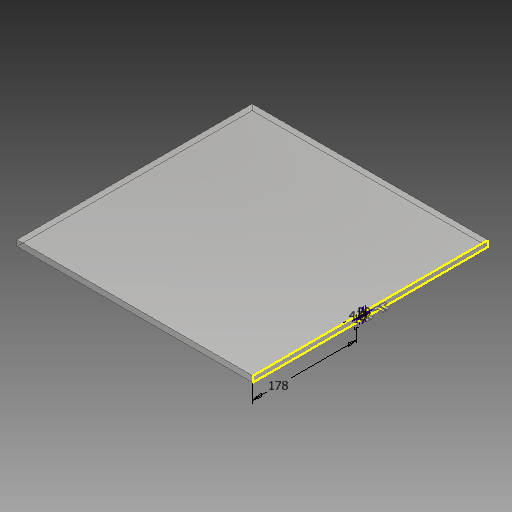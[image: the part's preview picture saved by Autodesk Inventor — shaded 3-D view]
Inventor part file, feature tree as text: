
AUTODESK INVENTOR PART (.ipt)
format: ipt  version: 2018.3 (Build 223284000, 284)  size: 160,768 bytes
history: native  units: mm
features: extrude x3, sketch x2, pattern_linear x1, projected_geometry x1
ambient origin geometry x8: Origin, YZ Plane, XZ Plane, XY Plane, X Axis, Y Axis, Z Axis, Center Point
bodies: Volumenkörper1 (feature_tree)
feature tree (7):
  extrude  "Extrusion1"  Depth=400.0mm
  sketch  "Skizze2"  dims[d2=10.0mm d3=0.0mm d4=20.0mm d5=1.0mm d6=11.0mm d7=2.0mm d8=4.5mm d10=178.0mm d11=4.0mm d12=0.0mm d15=13.0mm d16=0.0mm d17=20.0mm d19=27.0mm]
  extrude  "Extrusion2"  Depth=20.0mm
  extrude  "Extrusion4"  Depth=1.0mm
  pattern_linear  "Rechteckige Anordnung1"  Spacing1=11.0mm  [1 undecoded]
  sketch  "Skizze1"  dims[d0=400.0mm d1=400.0mm]
  projected_geometry  "Projizierte Kontur1"
note: 1 required parameter value undecoded (feature->parameter linkage not recoverable at this tier; creation-order binding heuristic only, values carry confidence <= 0.55)
